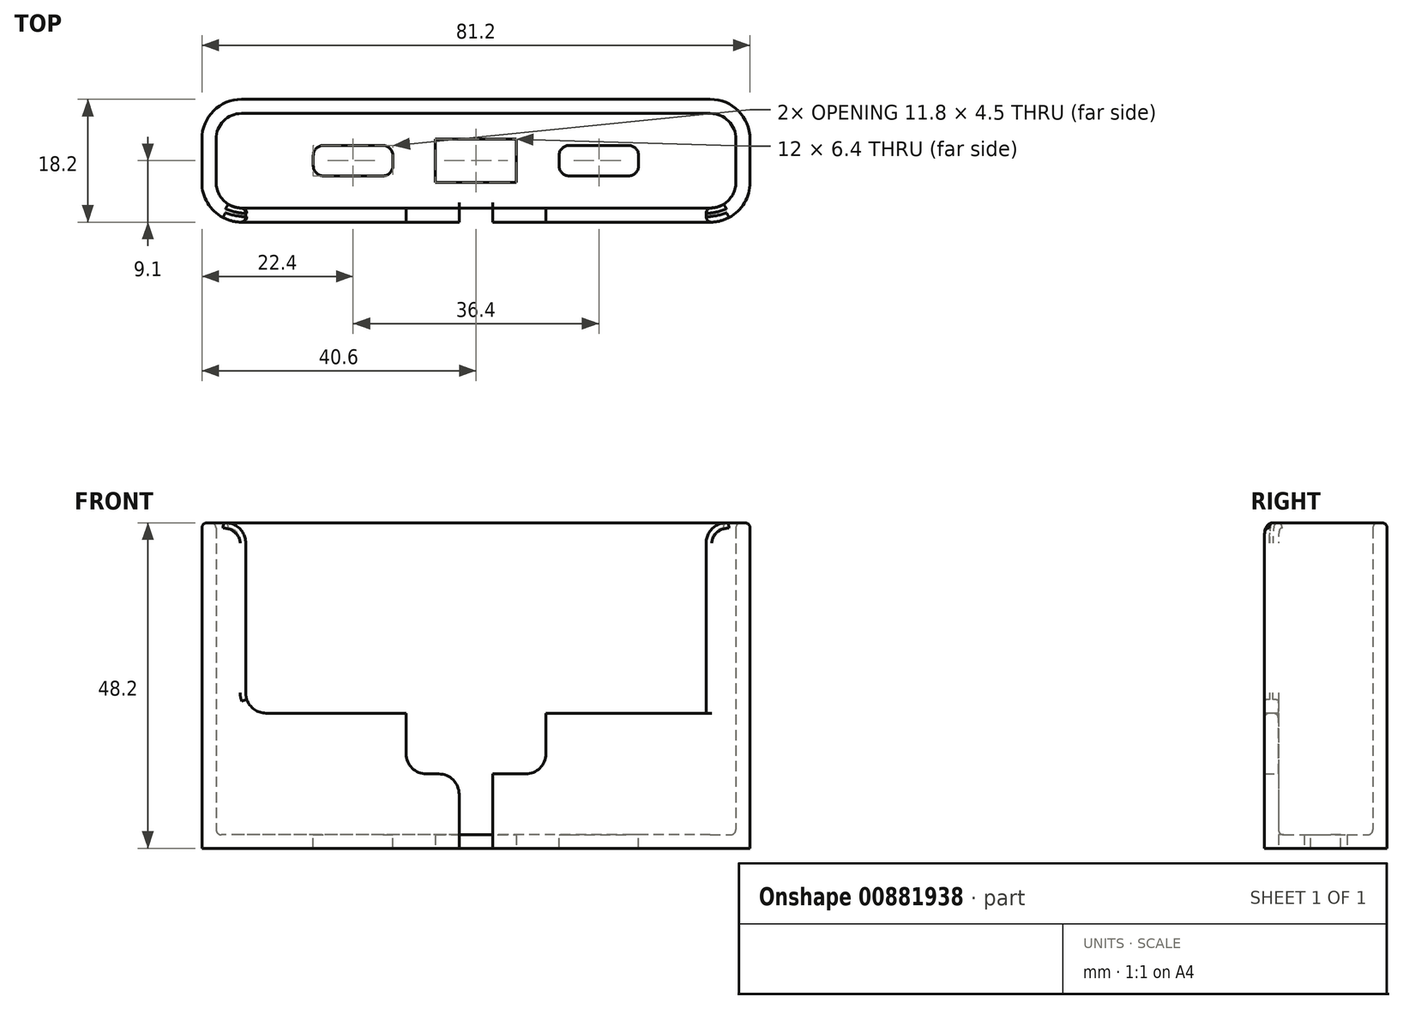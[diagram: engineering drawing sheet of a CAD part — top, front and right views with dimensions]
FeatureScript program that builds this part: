
annotation { "Feature Type Name" : "Feature", "Feature Type Description" : "" }
export const myFeature = defineFeature(function(context is Context, id is Id, definition is map)
    precondition{}
    {
        {
            var Q0;
            Q0=qCreatedBy(makeId("Top.planeOp"),FACE);
            var sketch = newSketch(context, id + "F0", { "sketchPlane" : qUnion([Q0])});
            skLineSegment(sketch, "E0", {"start": v(-34.7, 14) * mm, "end": v(34.7, 14) * mm});
            skLineSegment(sketch, "E1", {"start": v(-34.7, 0) * mm, "end": v(34.7, 0) * mm});
            skLineSegment(sketch, "E2", {"start": v(-38.5, 10.2) * mm, "end": v(-38.5, 3.8) * mm});
            skLineSegment(sketch, "E3", {"start": v(38.5, 10.2) * mm, "end": v(38.5, 3.8) * mm});
            skLineSegment(sketch, "E4", {"start": v(0, 0) * mm, "end": v(0, 38.88) * mm, "construction": true});
            skLineSegment(sketch, "E5.0", {"start": v(-34.7, 16.1) * mm, "end": v(34.7, 16.1) * mm});
            skLineSegment(sketch, "E5.1", {"start": v(-40.6, 10.2) * mm, "end": v(-40.6, 3.8) * mm});
            skLineSegment(sketch, "E5.2", {"start": v(-34.7, -2.1) * mm, "end": v(34.7, -2.1) * mm});
            skLineSegment(sketch, "E5.3", {"start": v(40.6, 10.2) * mm, "end": v(40.6, 3.8) * mm});
            skPoint(sketch, "E6.visualSharp", {"position": v(-38.5, 14) * mm});
            skArc(sketch, "E6.filletArc", {"start": v(-34.7, 14) * mm, "mid": v(-37.39, 12.89) * mm, "end": v(-38.5, 10.2) * mm});
            skPoint(sketch, "E7.visualSharp", {"position": v(-38.5, 0) * mm});
            skArc(sketch, "E7.filletArc", {"start": v(-38.5, 3.8) * mm, "mid": v(-37.39, 1.11) * mm, "end": v(-34.7, 0) * mm});
            skPoint(sketch, "E8.visualSharp", {"position": v(38.5, 0) * mm});
            skArc(sketch, "E8.filletArc", {"start": v(34.7, 0) * mm, "mid": v(37.39, 1.11) * mm, "end": v(38.5, 3.8) * mm});
            skPoint(sketch, "E9.visualSharp", {"position": v(38.5, 14) * mm});
            skArc(sketch, "E9.filletArc", {"start": v(38.5, 10.2) * mm, "mid": v(37.39, 12.89) * mm, "end": v(34.7, 14) * mm});
            skPoint(sketch, "E10.visualSharp", {"position": v(-40.6, 16.1) * mm});
            skArc(sketch, "E10.filletArc", {"start": v(-34.7, 16.1) * mm, "mid": v(-38.87, 14.37) * mm, "end": v(-40.6, 10.2) * mm});
            skPoint(sketch, "E11.visualSharp", {"position": v(-40.6, -2.1) * mm});
            skArc(sketch, "E11.filletArc", {"start": v(-40.6, 3.8) * mm, "mid": v(-38.87, -0.37) * mm, "end": v(-34.7, -2.1) * mm});
            skPoint(sketch, "E12.visualSharp", {"position": v(40.6, -2.1) * mm});
            skArc(sketch, "E12.filletArc", {"start": v(34.7, -2.1) * mm, "mid": v(38.87, -0.37) * mm, "end": v(40.6, 3.8) * mm});
            skPoint(sketch, "E13.visualSharp", {"position": v(40.6, 16.1) * mm});
            skArc(sketch, "E13.filletArc", {"start": v(40.6, 10.2) * mm, "mid": v(38.87, 14.37) * mm, "end": v(34.7, 16.1) * mm});
            skSolve(sketch);
        }
        {
            var Q0;
            Q0=makeQuery(id+"F0.imprint","IMPRINT",FACE,{"disambiguationData":[TD([[makeQuery(id+"F0.imprint","IMPRINT",EDGE,{"derivedFrom":sQuery(id+"F0.wireOp",EDGE,"E0")}),1.0]])]});
            var Q1;
            Q1=makeQuery(id+"F0.imprint","IMPRINT",FACE,{"disambiguationData":[TD([[makeQuery(id+"F0.imprint","IMPRINT",EDGE,{"derivedFrom":sQuery(id+"F0.wireOp",EDGE,"E0")}),-1.0]])]});
            extrude(context, id + "F1", {"entities" : qUnion([Q0, Q1]), "depth" : 2 * mm, "offsetDistance" : 25 * mm});
        }
        {
            var Q0;
            Q0=makeQuery(id+"F0.imprint","IMPRINT",FACE,{"disambiguationData":[TD([[makeQuery(id+"F0.imprint","IMPRINT",EDGE,{"derivedFrom":sQuery(id+"F0.wireOp",EDGE,"E0")}),1.0]])]});
            extrude(context, id + "F2", {"entities" : qUnion([Q0]), "operationType" : NewBodyOperationType.ADD, "depth" : 20 * mm, "offsetDistance" : 25 * mm});
        }
        {
            var Q0;
            {var subQ0=sQuery(id+"F0.wireOp",EDGE,"E5.2");Q0=makeQuery(id+"F2.boolean.opBoolean","MERGE",FACE,{"derivedFrom":[makeQuery(id+"F1.opExtrude","SWEPT_FACE",FACE,{"disambiguationData":[OSD([subQ0])]}),makeQuery(id+"F2.opExtrude","SWEPT_FACE",FACE,{"disambiguationData":[OSD([subQ0])]})]});}
            var sketch = newSketch(context, id + "F3", { "sketchPlane" : qUnion([Q0])});
            skLineSegment(sketch, "E14.bottom", {"start": v(10.35, 11) * mm, "end": v(-10.35, 11) * mm});
            skLineSegment(sketch, "E14.top", {"start": v(10.35, 29) * mm, "end": v(-10.35, 29) * mm});
            skLineSegment(sketch, "E14.left", {"start": v(10.35, 11) * mm, "end": v(10.35, 29) * mm});
            skLineSegment(sketch, "E14.right", {"start": v(-10.35, 11) * mm, "end": v(-10.35, 29) * mm});
            skPoint(sketch, "E14.middle", {"position": v(0, 20) * mm});
            skSolve(sketch);
        }
        {
            var Q0;
            {var subQ0=sQuery(id+"F3.wireOp",EDGE,"E14.bottom");Q0=makeQuery(id+"F3.imprint","IMPRINT",FACE,{"disambiguationData":[TD([[makeQuery(id+"F3.imprint","IMPRINT",EDGE,{"derivedFrom":subQ0}),-1.0]])]});}
            extrude(context, id + "F4", {"entities" : qUnion([Q0]), "operationType" : NewBodyOperationType.REMOVE, "endBound" : BoundingType.UP_TO_NEXT, "oppositeDirection" : true, "depth" : 25 * mm, "offsetDistance" : 25 * mm});
        }
        {
            var Q0;
            Q0=makeQuery(id+"F2.opExtrude","CAP_FACE",FACE,{"disambiguationData":[OSD([sQuery(id+"F0.wireOp",EDGE,"E0"),sQuery(id+"F0.wireOp",EDGE,"E1"),sQuery(id+"F0.wireOp",EDGE,"E2"),sQuery(id+"F0.wireOp",EDGE,"E3"),sQuery(id+"F0.wireOp",EDGE,"E5.0"),sQuery(id+"F0.wireOp",EDGE,"E5.1"),sQuery(id+"F0.wireOp",EDGE,"E5.2"),sQuery(id+"F0.wireOp",EDGE,"E5.3"),sQuery(id+"F0.wireOp",EDGE,"E6.filletArc"),sQuery(id+"F0.wireOp",EDGE,"E7.filletArc"),sQuery(id+"F0.wireOp",EDGE,"E8.filletArc"),sQuery(id+"F0.wireOp",EDGE,"E9.filletArc"),sQuery(id+"F0.wireOp",EDGE,"E10.filletArc"),sQuery(id+"F0.wireOp",EDGE,"E11.filletArc"),sQuery(id+"F0.wireOp",EDGE,"E12.filletArc"),sQuery(id+"F0.wireOp",EDGE,"E13.filletArc")])],"isStart":false});
            var sketch = newSketch(context, id + "F5", { "sketchPlane" : qUnion([Q0])});
            skLineSegment(sketch, "E15", {"start": v(-34.1, 0) * mm, "end": v(-34.1, -2.1) * mm});
            skLineSegment(sketch, "E16.MirrorCS", {"start": v(34.1, 0) * mm, "end": v(34.1, -2.1) * mm});
            skSolve(sketch);
        }
        {
            var Q0;
            {var subQ7=sQuery(id+"F5.wireOp",EDGE,"E15");Q0=makeQuery(id+"F5.imprint","IMPRINT",FACE,{"disambiguationData":[TD([[makeQuery(id+"F5.imprint","IMPRINT",EDGE,{"derivedFrom":subQ7}),-1.0]])]});}
            extrude(context, id + "F6", {"entities" : qUnion([Q0]), "operationType" : NewBodyOperationType.ADD, "depth" : 28.2 * mm, "offsetDistance" : 25 * mm});
        }
        {
            var Q0;
            Q0=makeQuery(id+"F1.opExtrude","CAP_FACE",FACE,{"disambiguationData":[OSD([sQuery(id+"F0.wireOp",EDGE,"E5.0"),sQuery(id+"F0.wireOp",EDGE,"E5.1"),sQuery(id+"F0.wireOp",EDGE,"E5.2"),sQuery(id+"F0.wireOp",EDGE,"E5.3"),sQuery(id+"F0.wireOp",EDGE,"E10.filletArc"),sQuery(id+"F0.wireOp",EDGE,"E11.filletArc"),sQuery(id+"F0.wireOp",EDGE,"E12.filletArc"),sQuery(id+"F0.wireOp",EDGE,"E13.filletArc")])],"isStart":false});
            var sketch = newSketch(context, id + "F7", { "sketchPlane" : qUnion([Q0])});
            skLineSegment(sketch, "E17", {"start": v(0, 14) * mm, "end": v(0, 0) * mm, "construction": true});
            skLineSegment(sketch, "E18.bottom", {"start": v(6, 3.8) * mm, "end": v(-6, 3.8) * mm});
            skLineSegment(sketch, "E18.top", {"start": v(6, 10.2) * mm, "end": v(-6, 10.2) * mm});
            skLineSegment(sketch, "E18.left", {"start": v(6, 3.8) * mm, "end": v(6, 10.2) * mm});
            skLineSegment(sketch, "E18.right", {"start": v(-6, 3.8) * mm, "end": v(-6, 10.2) * mm});
            skPoint(sketch, "E18.middle", {"position": v(0, 7) * mm});
            skLineSegment(sketch, "E19.bottom", {"start": v(2.5, -2.1) * mm, "end": v(-2.5, -2.1) * mm});
            skLineSegment(sketch, "E19.top", {"start": v(2.5, 3.8) * mm, "end": v(-2.5, 3.8) * mm});
            skLineSegment(sketch, "E19.left", {"start": v(2.5, -2.1) * mm, "end": v(2.5, 3.8) * mm});
            skLineSegment(sketch, "E19.right", {"start": v(-2.5, -2.1) * mm, "end": v(-2.5, 3.8) * mm});
            skPoint(sketch, "E19.middle", {"position": v(0, 0.85) * mm});
            skSolve(sketch);
        }
        {
            var Q0;
            Q0=makeQuery(id+"F7.imprint","IMPRINT",FACE,{"disambiguationData":[TD([[makeQuery(id+"F7.imprint","IMPRINT",EDGE,{"derivedFrom":sQuery(id+"F7.wireOp",EDGE,"E18.top")}),1.0]])]});
            var Q1;
            {var subQ0=sQuery(id+"F7.wireOp",EDGE,"E19.top");Q1=makeQuery(id+"F7.imprint","IMPRINT",FACE,{"disambiguationData":[TD([[makeQuery(id+"F7.imprint","IMPRINT",EDGE,{"derivedFrom":subQ0}),1.0]])]});}
            var Q2;
            {var subQ0=sQuery(id+"F7.wireOp",EDGE,"E19.bottom");Q2=makeQuery(id+"F7.imprint","IMPRINT",FACE,{"disambiguationData":[TD([[makeQuery(id+"F7.imprint","IMPRINT",EDGE,{"derivedFrom":subQ0}),-1.0]])]});}
            var Q3;
            Q3=makeQuery(id+"F4.boolean.opBoolean","COPY",FACE,{"derivedFrom":makeQuery(id+"F4.opExtrude","SWEPT_FACE",FACE,{"disambiguationData":[OSD([sQuery(id+"F3.wireOp",EDGE,"E14.bottom")])]})});
            var Q4;
            Q4=makeQuery(id+"F1.opExtrude","CAP_FACE",FACE,{"disambiguationData":[OSD([sQuery(id+"F0.wireOp",EDGE,"E5.0"),sQuery(id+"F0.wireOp",EDGE,"E5.1"),sQuery(id+"F0.wireOp",EDGE,"E5.2"),sQuery(id+"F0.wireOp",EDGE,"E5.3"),sQuery(id+"F0.wireOp",EDGE,"E10.filletArc"),sQuery(id+"F0.wireOp",EDGE,"E11.filletArc"),sQuery(id+"F0.wireOp",EDGE,"E12.filletArc"),sQuery(id+"F0.wireOp",EDGE,"E13.filletArc")])],"isStart":true});
            extrude(context, id + "F8", {"entities" : qUnion([Q0, Q1, Q2]), "operationType" : NewBodyOperationType.REMOVE, "endBound" : BoundingType.UP_TO_SURFACE, "depth" : 25 * mm, "endBoundEntityFace" : qUnion([Q3]), "offsetDistance" : 25 * mm, "hasSecondDirection" : true, "secondDirectionBound" : SecondDirectionBoundingType.UP_TO_SURFACE, "secondDirectionOppositeDirection" : true, "secondDirectionDepth" : 25 * mm, "secondDirectionBoundEntityFace" : qUnion([Q4])});
        }
        {
            var Q0;
            Q0=makeQuery(id+"F1.opExtrude","CAP_FACE",FACE,{"disambiguationData":[OSD([sQuery(id+"F0.wireOp",EDGE,"E5.0"),sQuery(id+"F0.wireOp",EDGE,"E5.1"),sQuery(id+"F0.wireOp",EDGE,"E5.2"),sQuery(id+"F0.wireOp",EDGE,"E5.3"),sQuery(id+"F0.wireOp",EDGE,"E10.filletArc"),sQuery(id+"F0.wireOp",EDGE,"E11.filletArc"),sQuery(id+"F0.wireOp",EDGE,"E12.filletArc"),sQuery(id+"F0.wireOp",EDGE,"E13.filletArc")])],"isStart":false});
            var sketch = newSketch(context, id + "F9", { "sketchPlane" : qUnion([Q0])});
            skLineSegment(sketch, "E20.bottom", {"start": v(-12.3, 4.75) * mm, "end": v(-24.1, 4.75) * mm});
            skLineSegment(sketch, "E20.top", {"start": v(-12.3, 9.25) * mm, "end": v(-24.1, 9.25) * mm});
            skLineSegment(sketch, "E20.left", {"start": v(-12.3, 4.75) * mm, "end": v(-12.3, 9.25) * mm});
            skLineSegment(sketch, "E20.right", {"start": v(-24.1, 4.75) * mm, "end": v(-24.1, 9.25) * mm});
            skPoint(sketch, "E20.middle", {"position": v(-18.2, 7) * mm});
            skPoint(sketch, "E20.middle.positionSnap0", {"position": v(-38.5, 7) * mm});
            skPoint(sketch, "E20.centerSnap0", {"position": v(-38.5, 7) * mm});
            skLineSegment(sketch, "E21.MirrorCS", {"start": v(12.3, 9.25) * mm, "end": v(24.1, 9.25) * mm});
            skLineSegment(sketch, "E22.MirrorCS", {"start": v(24.1, 4.75) * mm, "end": v(24.1, 9.25) * mm});
            skLineSegment(sketch, "E23.MirrorCS", {"start": v(12.3, 4.75) * mm, "end": v(24.1, 4.75) * mm});
            skLineSegment(sketch, "E24.MirrorCS", {"start": v(12.3, 4.75) * mm, "end": v(12.3, 9.25) * mm});
            skSolve(sketch);
        }
        {
            var Q0;
            Q0=makeQuery(id+"F9.imprint","IMPRINT",FACE,{"disambiguationData":[TD([[makeQuery(id+"F9.imprint","IMPRINT",EDGE,{"derivedFrom":sQuery(id+"F9.wireOp",EDGE,"E20.bottom")}),-1.0]])]});
            var Q1;
            Q1=makeQuery(id+"F9.imprint","IMPRINT",FACE,{"disambiguationData":[TD([[makeQuery(id+"F9.imprint","IMPRINT",EDGE,{"derivedFrom":sQuery(id+"F9.wireOp",EDGE,"E21.MirrorCS")}),-1.0]])]});
            var Q2;
            Q2=makeQuery(id+"F1.opExtrude","CAP_FACE",FACE,{"disambiguationData":[OSD([sQuery(id+"F0.wireOp",EDGE,"E5.0"),sQuery(id+"F0.wireOp",EDGE,"E5.1"),sQuery(id+"F0.wireOp",EDGE,"E5.2"),sQuery(id+"F0.wireOp",EDGE,"E5.3"),sQuery(id+"F0.wireOp",EDGE,"E10.filletArc"),sQuery(id+"F0.wireOp",EDGE,"E11.filletArc"),sQuery(id+"F0.wireOp",EDGE,"E12.filletArc"),sQuery(id+"F0.wireOp",EDGE,"E13.filletArc")])],"isStart":true});
            extrude(context, id + "F10", {"entities" : qUnion([Q0, Q1]), "operationType" : NewBodyOperationType.REMOVE, "endBound" : BoundingType.UP_TO_SURFACE, "oppositeDirection" : true, "depth" : 25 * mm, "endBoundEntityFace" : qUnion([Q2]), "offsetDistance" : 25 * mm});
        }
        {
            var Q0;
            Q0=makeQuery(id+"F6.opExtrude","CAP_EDGE",EDGE,{"disambiguationData":[OSD([sQuery(id+"F5.wireOp",EDGE,"E15")])],"isStart":false});
            var Q1;
            Q1=makeQuery(id+"F6.opExtrude","CAP_EDGE",EDGE,{"disambiguationData":[OSD([sQuery(id+"F5.wireOp",EDGE,"E16.MirrorCS")])],"isStart":false});
            var Q2;
            Q2=makeQuery(id+"F6.opExtrude","CAP_EDGE",EDGE,{"disambiguationData":[OSD([sQuery(id+"F5.wireOp",EDGE,"E15")])],"isStart":true});
            var Q3;
            Q3=makeQuery(id+"F6.opExtrude","CAP_EDGE",EDGE,{"disambiguationData":[OSD([sQuery(id+"F5.wireOp",EDGE,"E16.MirrorCS")])],"isStart":true});
            var Q4;
            Q4=makeQuery(id+"F4.boolean.opBoolean","COPY",EDGE,{"derivedFrom":makeQuery(id+"F4.opExtrude","SWEPT_EDGE",EDGE,{"disambiguationData":[OSD([sQuery(id+"F0.wireOp",EDGE,"E5.2"),sQuery(id+"F3.wireOp",EDGE,"E14.right")])]})});
            var Q5;
            Q5=makeQuery(id+"F4.boolean.opBoolean","COPY",EDGE,{"derivedFrom":makeQuery(id+"F4.opExtrude","SWEPT_EDGE",EDGE,{"disambiguationData":[OSD([sQuery(id+"F0.wireOp",EDGE,"E5.2"),sQuery(id+"F3.wireOp",EDGE,"E14.left")])]})});
            var Q6;
            Q6=makeQuery(id+"F4.boolean.opBoolean","COPY",EDGE,{"derivedFrom":makeQuery(id+"F4.opExtrude","SWEPT_EDGE",EDGE,{"disambiguationData":[OSD([sQuery(id+"F3.wireOp",EDGE,"E14.bottom"),sQuery(id+"F3.wireOp",EDGE,"E14.left")])]})});
            var Q7;
            Q7=makeQuery(id+"F4.boolean.opBoolean","COPY",EDGE,{"derivedFrom":makeQuery(id+"F4.opExtrude","SWEPT_EDGE",EDGE,{"disambiguationData":[OSD([sQuery(id+"F3.wireOp",EDGE,"E14.bottom"),sQuery(id+"F3.wireOp",EDGE,"E14.right")])]})});
            var Q8;
            Q8=makeQuery(id+"F8.boolean.opBoolean","COPY",EDGE,{"derivedFrom":makeQuery(id+"F8.opExtrude","CAP_EDGE",EDGE,{"disambiguationData":[OSD([sQuery(id+"F7.wireOp",EDGE,"E19.right")])],"isStart":false})});
            var Q9;
            Q9=makeQuery(id+"F8.boolean.opBoolean","COPY",EDGE,{"derivedFrom":makeQuery(id+"F8.opExtrude","CAP_EDGE",EDGE,{"disambiguationData":[OSD([sQuery(id+"F7.wireOp",EDGE,"E19.left")])],"isStart":false})});
            fillet(context, id + "F11", {"entities" : qUnion([Q0, Q1, Q2, Q3, Q4, Q5, Q6, Q7, Q8, Q9]), "radius" : 3 * mm, "tangentPropagation" : true, "allowEdgeOverflow" : false});
        }
        {
            var Q0;
            Q0=makeQuery(id+"F10.boolean.opBoolean","COPY",EDGE,{"derivedFrom":makeQuery(id+"F10.opExtrude","SWEPT_EDGE",EDGE,{"disambiguationData":[OSD([sQuery(id+"F9.wireOp",EDGE,"E20.bottom"),sQuery(id+"F9.wireOp",EDGE,"E20.right")])]})});
            var Q1;
            {var subQ0=sQuery(id+"F7.wireOp",EDGE,"E18.right");var subQ1=sQuery(id+"F7.wireOp",EDGE,"E18.bottom");Q1=makeQuery(id+"F8.boolean.opBoolean","COPY",EDGE,{"derivedFrom":makeQuery(id+"F8.opExtrude","TWEAK_EDGE",EDGE,{"derivedFrom":[makeQuery(id+"F7.imprint","IMPRINT",EDGE,{"disambiguationData":[TD([[makeQuery(id+"F7.imprint","INTERSECT",VERTEX,{"derivedFrom":[subQ1,subQ0]}),1.0]])],"derivedFrom":subQ1}),makeQuery(id+"F7.imprint","IMPRINT",EDGE,{"derivedFrom":subQ0})]})});}
            var Q2;
            Q2=makeQuery(id+"F10.boolean.opBoolean","COPY",EDGE,{"derivedFrom":makeQuery(id+"F10.opExtrude","SWEPT_EDGE",EDGE,{"disambiguationData":[OSD([sQuery(id+"F9.wireOp",EDGE,"E23.MirrorCS"),sQuery(id+"F9.wireOp",EDGE,"E24.MirrorCS")])]})});
            var Q3;
            Q3=makeQuery(id+"F10.boolean.opBoolean","COPY",EDGE,{"derivedFrom":makeQuery(id+"F10.opExtrude","SWEPT_EDGE",EDGE,{"disambiguationData":[OSD([sQuery(id+"F9.wireOp",EDGE,"E22.MirrorCS"),sQuery(id+"F9.wireOp",EDGE,"E23.MirrorCS")])]})});
            var Q4;
            {var subQ0=sQuery(id+"F7.wireOp",EDGE,"E18.left");var subQ1=sQuery(id+"F7.wireOp",EDGE,"E18.bottom");Q4=makeQuery(id+"F8.boolean.opBoolean","COPY",EDGE,{"derivedFrom":makeQuery(id+"F8.opExtrude","TWEAK_EDGE",EDGE,{"derivedFrom":[makeQuery(id+"F7.imprint","IMPRINT",EDGE,{"disambiguationData":[TD([[makeQuery(id+"F7.imprint","INTERSECT",VERTEX,{"derivedFrom":[subQ1,subQ0]}),-1.0]])],"derivedFrom":subQ1}),makeQuery(id+"F7.imprint","IMPRINT",EDGE,{"derivedFrom":subQ0})]})});}
            var Q5;
            Q5=makeQuery(id+"F10.boolean.opBoolean","COPY",EDGE,{"derivedFrom":makeQuery(id+"F10.opExtrude","SWEPT_EDGE",EDGE,{"disambiguationData":[OSD([sQuery(id+"F9.wireOp",EDGE,"E20.top"),sQuery(id+"F9.wireOp",EDGE,"E20.left")])]})});
            var Q6;
            Q6=makeQuery(id+"F8.boolean.opBoolean","COPY",EDGE,{"derivedFrom":makeQuery(id+"F8.opExtrude","TWEAK_EDGE",EDGE,{"derivedFrom":[makeQuery(id+"F7.imprint","IMPRINT",EDGE,{"derivedFrom":sQuery(id+"F7.wireOp",EDGE,"E18.top")}),makeQuery(id+"F7.imprint","IMPRINT",EDGE,{"derivedFrom":sQuery(id+"F7.wireOp",EDGE,"E18.left")})]})});
            var Q7;
            Q7=makeQuery(id+"F10.boolean.opBoolean","COPY",EDGE,{"derivedFrom":makeQuery(id+"F10.opExtrude","SWEPT_EDGE",EDGE,{"disambiguationData":[OSD([sQuery(id+"F9.wireOp",EDGE,"E21.MirrorCS"),sQuery(id+"F9.wireOp",EDGE,"E22.MirrorCS")])]})});
            var Q8;
            Q8=makeQuery(id+"F8.boolean.opBoolean","COPY",EDGE,{"derivedFrom":makeQuery(id+"F8.opExtrude","TWEAK_EDGE",EDGE,{"derivedFrom":[makeQuery(id+"F7.imprint","IMPRINT",EDGE,{"derivedFrom":sQuery(id+"F7.wireOp",EDGE,"E18.top")}),makeQuery(id+"F7.imprint","IMPRINT",EDGE,{"derivedFrom":sQuery(id+"F7.wireOp",EDGE,"E18.right")})]})});
            var Q9;
            Q9=makeQuery(id+"F10.boolean.opBoolean","COPY",EDGE,{"derivedFrom":makeQuery(id+"F10.opExtrude","SWEPT_EDGE",EDGE,{"disambiguationData":[OSD([sQuery(id+"F9.wireOp",EDGE,"E21.MirrorCS"),sQuery(id+"F9.wireOp",EDGE,"E24.MirrorCS")])]})});
            var Q10;
            Q10=makeQuery(id+"F10.boolean.opBoolean","COPY",EDGE,{"derivedFrom":makeQuery(id+"F10.opExtrude","SWEPT_EDGE",EDGE,{"disambiguationData":[OSD([sQuery(id+"F9.wireOp",EDGE,"E20.top"),sQuery(id+"F9.wireOp",EDGE,"E20.right")])]})});
            var Q11;
            {var subQ0=sQuery(id+"F7.wireOp",EDGE,"E19.right");var subQ1=sQuery(id+"F7.wireOp",EDGE,"E18.bottom");var subQ2=makeQuery(id+"F7.imprint","INTERSECT",VERTEX,{"derivedFrom":[subQ1,sQuery(id+"F7.wireOp",EDGE,"E19.top"),subQ0]});Q11=makeQuery(id+"F8.boolean.opBoolean","COPY",EDGE,{"derivedFrom":makeQuery(id+"F8.opExtrude","TWEAK_EDGE",EDGE,{"derivedFrom":[makeQuery(id+"F7.imprint","IMPRINT",EDGE,{"disambiguationData":[TD([[makeQuery(id+"F7.imprint","INTERSECT",VERTEX,{"derivedFrom":[subQ1,sQuery(id+"F7.wireOp",EDGE,"E18.right")]}),1.0]])],"derivedFrom":subQ1}),makeQuery(id+"F7.imprint","IMPRINT",EDGE,{"disambiguationData":[TD([[makeQuery(id+"F7.imprint","INTERSECT",VERTEX,{"derivedFrom":[sQuery(id+"F7.wireOp",EDGE,"E19.bottom"),subQ0]}),-1.0]])],"derivedFrom":subQ0}),makeQuery(id+"F7.imprint","IMPRINT",EDGE,{"disambiguationData":[TD([[subQ2,1.0]])],"derivedFrom":subQ0})]})});}
            var Q12;
            {var subQ0=sQuery(id+"F7.wireOp",EDGE,"E19.left");var subQ1=sQuery(id+"F7.wireOp",EDGE,"E18.bottom");var subQ2=makeQuery(id+"F7.imprint","INTERSECT",VERTEX,{"derivedFrom":[subQ1,sQuery(id+"F7.wireOp",EDGE,"E19.top"),subQ0]});Q12=makeQuery(id+"F8.boolean.opBoolean","COPY",EDGE,{"derivedFrom":makeQuery(id+"F8.opExtrude","TWEAK_EDGE",EDGE,{"derivedFrom":[makeQuery(id+"F7.imprint","IMPRINT",EDGE,{"disambiguationData":[TD([[makeQuery(id+"F7.imprint","INTERSECT",VERTEX,{"derivedFrom":[subQ1,sQuery(id+"F7.wireOp",EDGE,"E18.left")]}),-1.0]])],"derivedFrom":subQ1}),makeQuery(id+"F7.imprint","IMPRINT",EDGE,{"disambiguationData":[TD([[makeQuery(id+"F7.imprint","INTERSECT",VERTEX,{"derivedFrom":[sQuery(id+"F7.wireOp",EDGE,"E19.bottom"),subQ0]}),-1.0]])],"derivedFrom":subQ0}),makeQuery(id+"F7.imprint","IMPRINT",EDGE,{"disambiguationData":[TD([[subQ2,1.0]])],"derivedFrom":subQ0})]})});}
            var Q13;
            Q13=makeQuery(id+"F10.boolean.opBoolean","COPY",EDGE,{"derivedFrom":makeQuery(id+"F10.opExtrude","SWEPT_EDGE",EDGE,{"disambiguationData":[OSD([sQuery(id+"F9.wireOp",EDGE,"E20.bottom"),sQuery(id+"F9.wireOp",EDGE,"E20.left")])]})});
            fillet(context, id + "F12", {"entities" : qUnion([Q0, Q1, Q2, Q3, Q4, Q5, Q6, Q7, Q8, Q9, Q10, Q11, Q12, Q13]), "radius" : 1.5 * mm, "tangentPropagation" : true, "allowEdgeOverflow" : false});
        }
        {
            var Q0;
            Q0=makeQuery(id+"F6.opExtrude","CAP_EDGE",EDGE,{"disambiguationData":[OSD([sQuery(id+"F0.wireOp",EDGE,"E5.0")])],"isStart":false});
            var Q1;
            Q1=makeQuery(id+"F6.opExtrude","CAP_EDGE",EDGE,{"disambiguationData":[OSD([sQuery(id+"F0.wireOp",EDGE,"E0")])],"isStart":false});
            var Q2;
            Q2=makeQuery(id+"F2.boolean.opBoolean","INTERSECT",EDGE,{"derivedFrom":[makeQuery(id+"F1.opExtrude","CAP_FACE",FACE,{"disambiguationData":[OSD([sQuery(id+"F0.wireOp",EDGE,"E5.0"),sQuery(id+"F0.wireOp",EDGE,"E5.1"),sQuery(id+"F0.wireOp",EDGE,"E5.2"),sQuery(id+"F0.wireOp",EDGE,"E5.3"),sQuery(id+"F0.wireOp",EDGE,"E10.filletArc"),sQuery(id+"F0.wireOp",EDGE,"E11.filletArc"),sQuery(id+"F0.wireOp",EDGE,"E12.filletArc"),sQuery(id+"F0.wireOp",EDGE,"E13.filletArc")])],"isStart":false}),makeQuery(id+"F2.opExtrude","SWEPT_FACE",FACE,{"disambiguationData":[OSD([sQuery(id+"F0.wireOp",EDGE,"E0")])]})]});
            fillet(context, id + "F13", {"entities" : qUnion([Q0, Q1, Q2]), "radius" : 0.8 * mm, "tangentPropagation" : true, "allowEdgeOverflow" : false});
        }
    });
